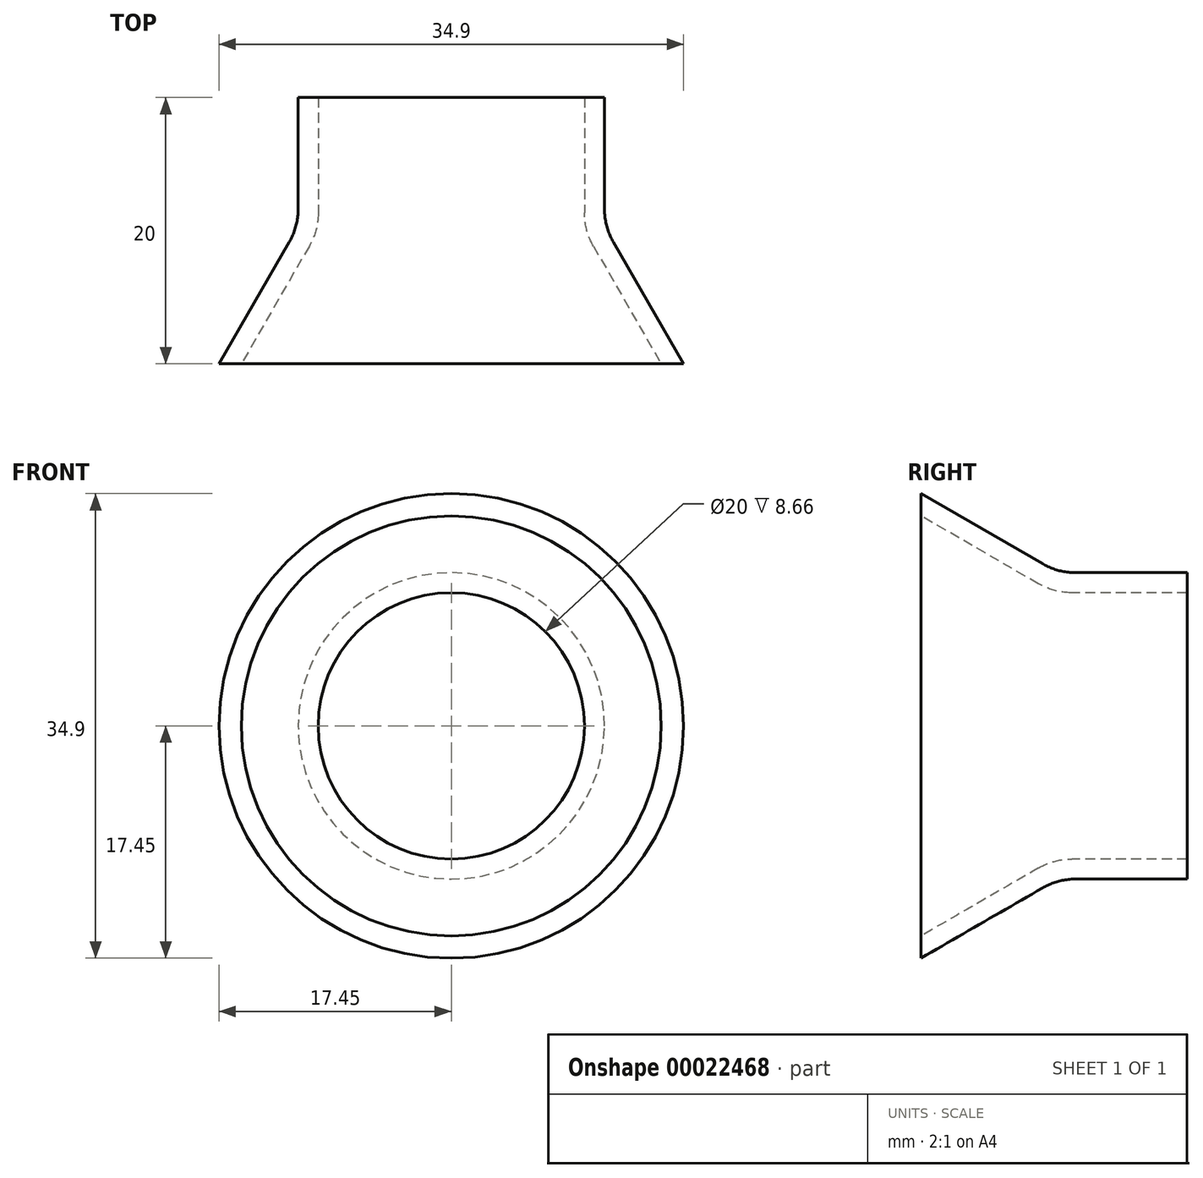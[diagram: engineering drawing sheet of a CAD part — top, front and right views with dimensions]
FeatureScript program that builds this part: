
annotation { "Feature Type Name" : "Feature", "Feature Type Description" : "" }
export const myFeature = defineFeature(function(context is Context, id is Id, definition is map)
    precondition{}
    {
        {
            var Q0;
            Q0=qCreatedBy(makeId("Right.planeOp"),FACE);
            var sketch = newSketch(context, id + "F0", { "sketchPlane" : qUnion([Q0])});
            skLineSegment(sketch, "E0", {"start": v(0, 0) * mm, "end": v(6.48, 0) * mm, "construction": true});
            skLineSegment(sketch, "E1", {"start": v(0, 10) * mm, "end": v(10, 10) * mm});
            skLineSegment(sketch, "E2", {"start": v(10, 10) * mm, "end": v(10, 11.5) * mm});
            skLineSegment(sketch, "E3", {"start": v(10, 11.5) * mm, "end": v(0.3, 11.5) * mm});
            skLineSegment(sketch, "E4", {"start": v(0.3, 11.5) * mm, "end": v(-10, 17.45) * mm});
            skLineSegment(sketch, "E5", {"start": v(-10, 17.45) * mm, "end": v(-10, 15.77) * mm});
            skLineSegment(sketch, "E6", {"start": v(-10, 15.77) * mm, "end": v(0, 10) * mm});
            skLineSegment(sketch, "E7", {"start": v(0.3, 11.5) * mm, "end": v(-0.09, 10.05) * mm, "construction": true});
            skPoint(sketch, "E8", {"position": v(10, -10) * mm});
            skSolve(sketch);
        }
        {
            var Q0;
            Q0=qSketchRegion(id+"F0",true);
            var Q1;
            Q1=sQuery(id+"F0.wireOp",EDGE,"E0");
            revolve(context, id + "F1", {"entities" : qUnion([Q0]), "axis" : qUnion([Q1]), "revolveType" : RevolveType.FULL});
        }
        {
            var Q0;
            Q0=makeQuery(id+"F1.opRevolve","SWEPT_EDGE",EDGE,{"disambiguationData":[OSD([sQuery(id+"F0.wireOp",EDGE,"E3"),sQuery(id+"F0.wireOp",EDGE,"E4")])]});
            var Q1;
            Q1=makeQuery(id+"F1.opRevolve","SWEPT_EDGE",EDGE,{"disambiguationData":[OSD([sQuery(id+"F0.wireOp",EDGE,"E1"),sQuery(id+"F0.wireOp",EDGE,"E6")])]});
            fillet(context, id + "F2", {"entities" : qUnion([Q0, Q1]), "radius" : 5 * mm, "tangentPropagation" : true, "allowEdgeOverflow" : false});
        }
    });
